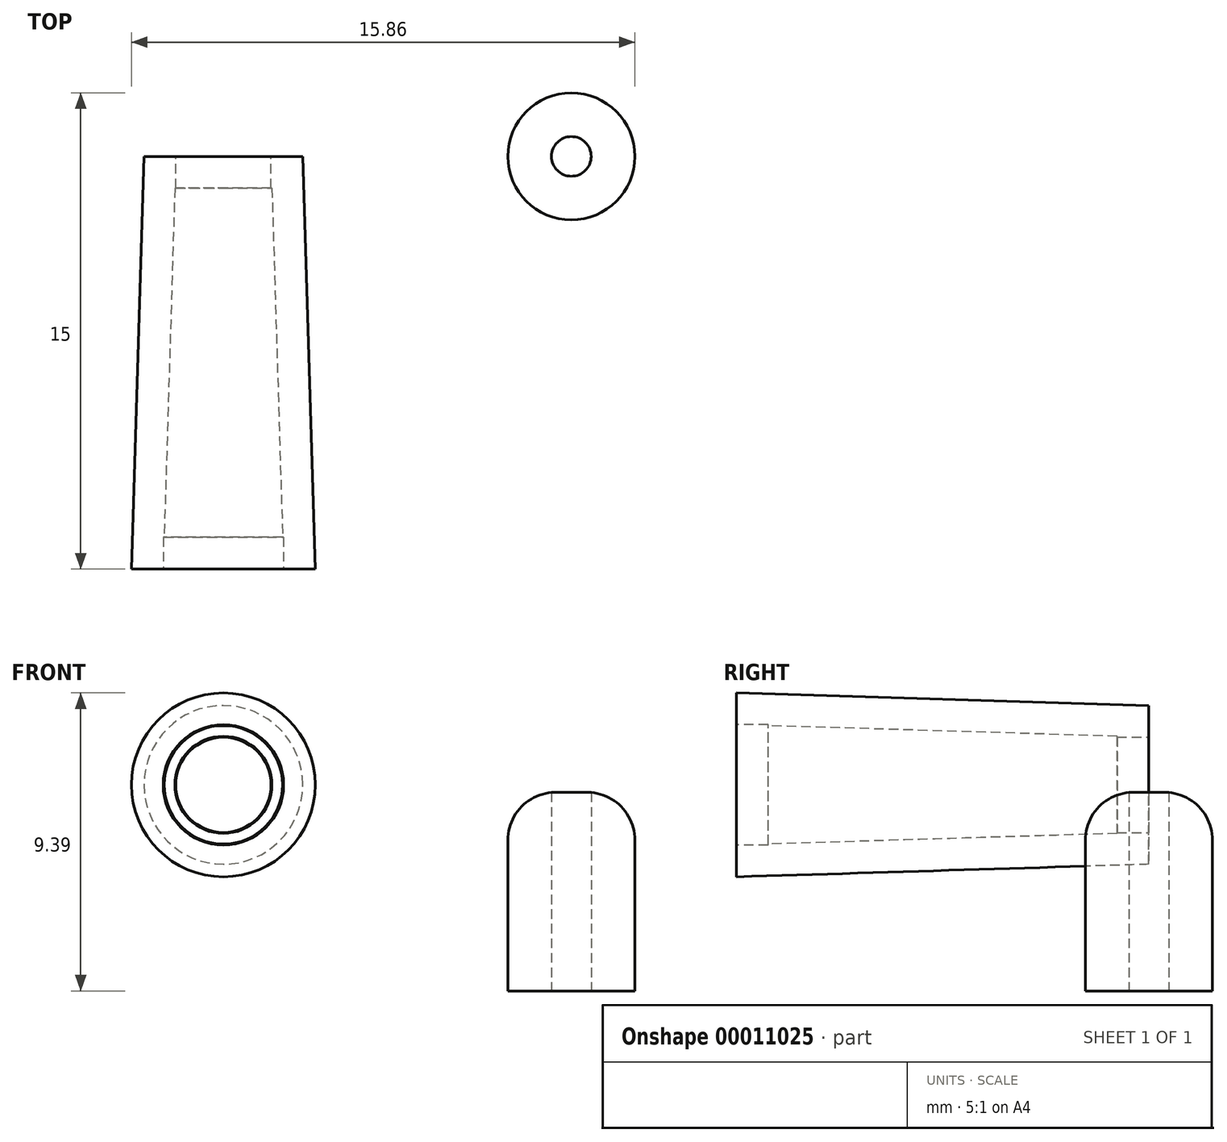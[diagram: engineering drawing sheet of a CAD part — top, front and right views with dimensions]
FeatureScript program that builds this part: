
annotation { "Feature Type Name" : "Feature", "Feature Type Description" : "" }
export const myFeature = defineFeature(function(context is Context, id is Id, definition is map)
    precondition{}
    {
        {
            var Q0;
            Q0=qCreatedBy(makeId("Top.planeOp"),FACE);
            var sketch = newSketch(context, id + "F0", { "sketchPlane" : qUnion([Q0])});
            skCircle(sketch, "E0", {"center": v(0, 0) * mm, "radius": 2 * mm});
            skCircle(sketch, "E1", {"center": v(0, 0) * mm, "radius": 0.62 * mm});
            skSolve(sketch);
        }
        {
            var Q0;
            Q0 = qSketchRegion(id + "F0", true);
            extrude(context, id + "F1", {"entities" : qUnion([Q0]), "depth" : 6.25 * mm});
        }
        {
            var Q0;
            Q0=makeQuery(id+"F1.opExtrude","CAP_EDGE",EDGE,{"disambiguationData":[OSD([sQuery(id+"F0.wireOp",EDGE,"E0")])],"isStart":false});
            fillet(context, id + "F2", {"entities" : qUnion([Q0]), "radius" : 1.5 * mm, "tangentPropagation" : true, "allowEdgeOverflow" : false});
        }
        {
            var Q0;
            Q0=qCreatedBy(makeId("Front.planeOp"),FACE);
            var sketch = newSketch(context, id + "F3", { "sketchPlane" : qUnion([Q0])});
            skCircle(sketch, "E2", {"center": v(-10.97, 6.5) * mm, "radius": 2.5 * mm});
            skSolve(sketch);
        }
        {
            var Q0;
            Q0 = qSketchRegion(id + "F3", true);
            extrude(context, id + "F4", {"entities" : qUnion([Q0]), "depth" : 13 * mm, "hasDraft" : true, "draftAngle" : 1.75 * degree});
        }
        {
            var Q0;
            Q0=makeQuery(id+"F4.opExtrude","CAP_FACE",FACE,{"disambiguationData":[OSD([sQuery(id+"F3.wireOp",EDGE,"E2")])],"isStart":false});
            var sketch = newSketch(context, id + "F5", { "sketchPlane" : qUnion([Q0])});
            skCircle(sketch, "E3", {"center": v(-10.97, 6.5) * mm, "radius": 2.9 * mm});
            skCircle(sketch, "E4", {"center": v(-10.97, 6.5) * mm, "radius": 1.9 * mm});
            skSolve(sketch);
        }
        {
            var Q0;
            Q0=makeQuery(id+"F4.opExtrude","CAP_FACE",FACE,{"disambiguationData":[OSD([sQuery(id+"F3.wireOp",EDGE,"E2")])],"isStart":false});
            var Q1;
            Q1=makeQuery(id+"F4.opExtrude","SWEPT_BODY",BODY,{"disambiguationData":[OSD([sQuery(id+"F3.wireOp",EDGE,"E2")])]});
            shell(context, id + "F6", {"isHollow" : true, "entities" : qUnion([Q0]), "parts" : qUnion([Q1]), "thickness" : 1 * mm});
        }
        {
            var Q0;
            Q0=makeQuery(id+"F5.imprint","IMPRINT",FACE,{"disambiguationData":[TD([[makeQuery(id+"F5.imprint","IMPRINT",EDGE,{"derivedFrom":sQuery(id+"F5.wireOp",EDGE,"E4")}),1.0]])]});
            extrude(context, id + "F7", {"entities" : qUnion([Q0]), "operationType" : NewBodyOperationType.REMOVE, "oppositeDirection" : true, "depth" : 1 * mm});
        }
        {
            var Q0;
            Q0=makeQuery(id+"F4.opExtrude","CAP_FACE",FACE,{"disambiguationData":[OSD([sQuery(id+"F3.wireOp",EDGE,"E2")])],"isStart":true});
            var sketch = newSketch(context, id + "F8", { "sketchPlane" : qUnion([Q0])});
            skCircle(sketch, "E5", {"center": v(10.97, 6.5) * mm, "radius": 1.5 * mm});
            skSolve(sketch);
        }
        {
            var Q0;
            Q0 = qSketchRegion(id + "F8", true);
            extrude(context, id + "F9", {"entities" : qUnion([Q0]), "operationType" : NewBodyOperationType.REMOVE, "oppositeDirection" : true, "depth" : 1 * mm});
        }
    });
